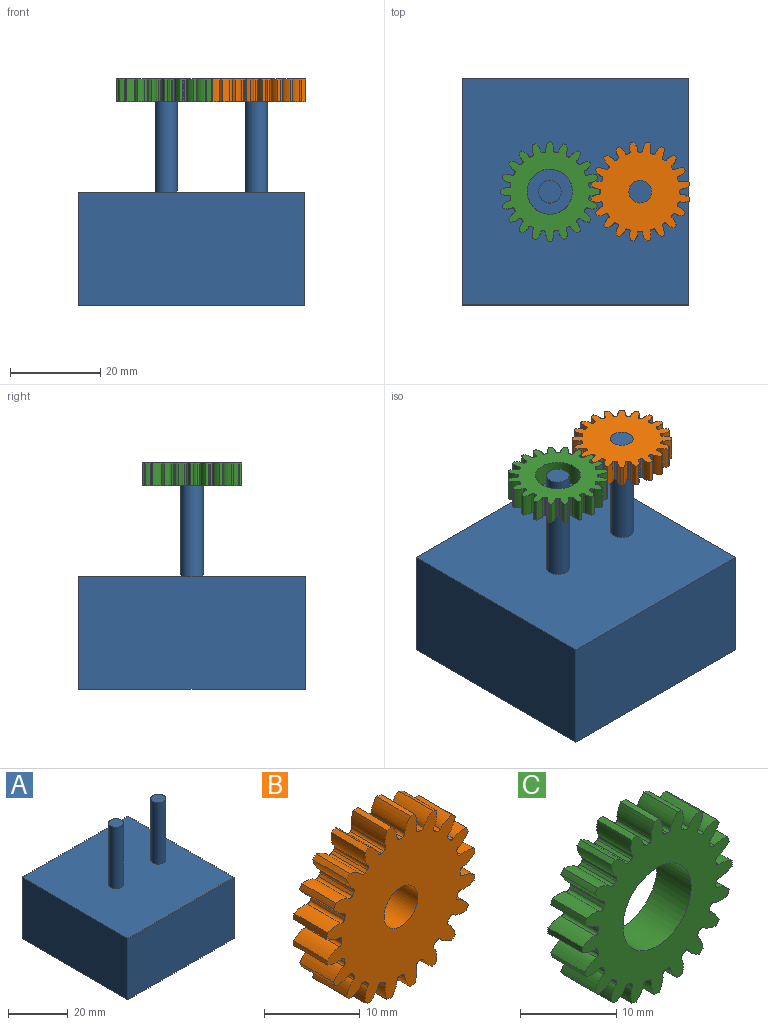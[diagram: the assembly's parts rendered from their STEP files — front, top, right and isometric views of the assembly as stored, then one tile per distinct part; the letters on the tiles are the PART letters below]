
ASSEMBLY  parts=3 mates=2
PART A: 10 faces, bbox 50x50x50 mm
  f0: plane 50x25mm, normal (-1,0,0), area 1250mm2, adj f1,f3,f4,f5
  f1: plane 50x25mm, normal (0,-1,0), area 1250mm2, adj f0,f2,f4,f5
  f2: plane 50x25mm, normal (1,0,0), area 1250mm2, adj f1,f3,f4,f5
  f3: plane 50x25mm, normal (0,1,0), area 1250mm2, adj f0,f2,f4,f5
  f4: plane 50x50mm, normal (0,0,1), area 2460.7mm2, adj f0,f1,f2,f3,f6,f8
  f5: plane 50x50mm, normal (0,0,-1), area 2500mm2, adj f0,f1,f2,f3
  f6: cylinder r=2.5mm len=25mm, axis (0,0,-1), area 392.7mm2, adj f4,f7
  f7: plane 5x5mm, normal (0,0,1), area 19.6mm2, adj f6
  f8: cylinder r=2.5mm len=25mm, axis (0,0,-1), area 392.7mm2, adj f4,f9
  f9: plane 5x5mm, normal (0,0,1), area 19.6mm2, adj f8
PART B: 123 faces, bbox 21.8x5x21.8 mm
  f0: extruded ~5x1.82mm, area 10.1mm2, adj f80,f81,f82,f83
  f1: cylinder r=8.75mm len=5mm, axis (0,1,0), area 2mm2, adj f81,f82,f83,f84
  f2: extruded ~5x1.82mm, area 10.1mm2, adj f3,f81,f82,f84
  f3: cylinder r=11mm len=5mm, axis (0,1,0), area 3.5mm2, adj f2,f4,f81,f82
  f4: extruded ~5x1.98mm, area 10.1mm2, adj f3,f81,f82,f85
  f5: cylinder r=8.75mm len=5mm, axis (0,1,0), area 2mm2, adj f81,f82,f85,f86
  f6: extruded ~5x1.48mm, area 10.1mm2, adj f7,f81,f82,f86
  f7: cylinder r=11mm len=5mm, axis (0,1,0), area 3.5mm2, adj f6,f8,f81,f82
  f8: extruded ~5x1.94mm, area 10.1mm2, adj f7,f81,f82,f87
  f9: cylinder r=8.75mm len=5mm, axis (0,1,0), area 2mm2, adj f81,f82,f87,f88
  f10: extruded ~5x1.71mm, area 10.1mm2, adj f11,f81,f82,f88
  f11: cylinder r=11mm len=5mm, axis (0,1,0), area 3.5mm2, adj f10,f12,f81,f82
  f12: extruded ~5x1.71mm, area 10.1mm2, adj f11,f81,f82,f89
  f13: cylinder r=8.75mm len=5mm, axis (0,1,0), area 2mm2, adj f81,f82,f89,f90
  f14: extruded ~5x1.94mm, area 10.1mm2, adj f15,f81,f82,f90
  f15: cylinder r=11mm len=5mm, axis (0,1,0), area 3.5mm2, adj f14,f16,f81,f82
  f16: extruded ~5x1.48mm, area 10.1mm2, adj f15,f81,f82,f91
  f17: cylinder r=8.75mm len=5mm, axis (0,1,0), area 2mm2, adj f81,f82,f91,f92
  f18: extruded ~5x1.98mm, area 10.1mm2, adj f19,f81,f82,f92
  f19: cylinder r=11mm len=5mm, axis (0,1,0), area 3.5mm2, adj f18,f20,f81,f82
  f20: extruded ~5x1.82mm, area 10.1mm2, adj f19,f81,f82,f93
  f21: cylinder r=8.75mm len=5mm, axis (0,1,0), area 2mm2, adj f81,f82,f93,f94
  f22: extruded ~5x1.82mm, area 10.1mm2, adj f23,f81,f82,f94
  f23: cylinder r=11mm len=5mm, axis (0,1,0), area 3.5mm2, adj f22,f24,f81,f82
  f24: extruded ~5x1.98mm, area 10.1mm2, adj f23,f81,f82,f95
  f25: cylinder r=8.75mm len=5mm, axis (0,1,0), area 2mm2, adj f81,f82,f95,f96
  f26: extruded ~5x1.48mm, area 10.1mm2, adj f27,f81,f82,f96
  f27: cylinder r=11mm len=5mm, axis (0,1,0), area 3.5mm2, adj f26,f28,f81,f82
  f28: extruded ~5x1.94mm, area 10.1mm2, adj f27,f81,f82,f97
  f29: cylinder r=8.75mm len=5mm, axis (0,1,0), area 2mm2, adj f81,f82,f97,f98
  f30: extruded ~5x1.71mm, area 10.1mm2, adj f31,f81,f82,f98
  f31: cylinder r=11mm len=5mm, axis (0,1,0), area 3.5mm2, adj f30,f32,f81,f82
  f32: extruded ~5x1.71mm, area 10.1mm2, adj f31,f81,f82,f99
  f33: cylinder r=8.75mm len=5mm, axis (0,1,0), area 2mm2, adj f81,f82,f99,f100
  f34: extruded ~5x1.94mm, area 10.1mm2, adj f35,f81,f82,f100
  f35: cylinder r=11mm len=5mm, axis (0,1,0), area 3.5mm2, adj f34,f36,f81,f82
  f36: extruded ~5x1.48mm, area 10.1mm2, adj f35,f81,f82,f101
  f37: cylinder r=8.75mm len=5mm, axis (0,1,0), area 2mm2, adj f81,f82,f101,f102
  f38: extruded ~5x1.98mm, area 10.1mm2, adj f39,f81,f82,f102
  f39: cylinder r=11mm len=5mm, axis (0,1,0), area 3.5mm2, adj f38,f40,f81,f82
  f40: extruded ~5x1.82mm, area 10.1mm2, adj f39,f81,f82,f103
  f41: cylinder r=8.75mm len=5mm, axis (0,1,0), area 2mm2, adj f81,f82,f103,f104
  f42: extruded ~5x1.82mm, area 10.1mm2, adj f43,f81,f82,f104
  f43: cylinder r=11mm len=5mm, axis (0,1,0), area 3.5mm2, adj f42,f44,f81,f82
  f44: extruded ~5x1.98mm, area 10.1mm2, adj f43,f81,f82,f105
  f45: cylinder r=8.75mm len=5mm, axis (0,1,0), area 2mm2, adj f81,f82,f105,f106
  f46: extruded ~5x1.48mm, area 10.1mm2, adj f47,f81,f82,f106
  f47: cylinder r=11mm len=5mm, axis (0,1,0), area 3.5mm2, adj f46,f48,f81,f82
  f48: extruded ~5x1.94mm, area 10.1mm2, adj f47,f81,f82,f107
  f49: cylinder r=8.75mm len=5mm, axis (0,1,0), area 2mm2, adj f81,f82,f107,f108
  f50: extruded ~5x1.71mm, area 10.1mm2, adj f51,f81,f82,f108
  f51: cylinder r=11mm len=5mm, axis (0,1,0), area 3.5mm2, adj f50,f52,f81,f82
  f52: extruded ~5x1.71mm, area 10.1mm2, adj f51,f81,f82,f109
  f53: cylinder r=8.75mm len=5mm, axis (0,1,0), area 2mm2, adj f81,f82,f109,f110
  f54: extruded ~5x1.94mm, area 10.1mm2, adj f55,f81,f82,f110
  f55: cylinder r=11mm len=5mm, axis (0,1,0), area 3.5mm2, adj f54,f56,f81,f82
  f56: extruded ~5x1.48mm, area 10.1mm2, adj f55,f81,f82,f111
  f57: cylinder r=8.75mm len=5mm, axis (0,1,0), area 2mm2, adj f81,f82,f111,f112
  f58: extruded ~5x1.98mm, area 10.1mm2, adj f59,f81,f82,f112
  f59: cylinder r=11mm len=5mm, axis (0,1,0), area 3.5mm2, adj f58,f60,f81,f82
  f60: extruded ~5x1.82mm, area 10.1mm2, adj f59,f81,f82,f113
  f61: cylinder r=8.75mm len=5mm, axis (0,1,0), area 2mm2, adj f81,f82,f113,f114
  f62: extruded ~5x1.82mm, area 10.1mm2, adj f63,f81,f82,f114
  f63: cylinder r=11mm len=5mm, axis (0,1,0), area 3.5mm2, adj f62,f64,f81,f82
  f64: extruded ~5x1.98mm, area 10.1mm2, adj f63,f81,f82,f115
  f65: cylinder r=8.75mm len=5mm, axis (0,1,0), area 2mm2, adj f81,f82,f115,f116
  f66: extruded ~5x1.48mm, area 10.1mm2, adj f67,f81,f82,f116
  f67: cylinder r=11mm len=5mm, axis (0,1,0), area 3.5mm2, adj f66,f68,f81,f82
  f68: extruded ~5x1.94mm, area 10.1mm2, adj f67,f81,f82,f117
  f69: cylinder r=8.75mm len=5mm, axis (0,1,0), area 2mm2, adj f81,f82,f117,f118
  f70: extruded ~5x1.71mm, area 10.1mm2, adj f71,f81,f82,f118
  f71: cylinder r=11mm len=5mm, axis (0,1,0), area 3.5mm2, adj f70,f72,f81,f82
  f72: extruded ~5x1.71mm, area 10.1mm2, adj f71,f81,f82,f119
  f73: cylinder r=8.75mm len=5mm, axis (0,1,0), area 2mm2, adj f81,f82,f119,f120
  f74: extruded ~5x1.94mm, area 10.1mm2, adj f75,f81,f82,f120
  f75: cylinder r=11mm len=5mm, axis (0,1,0), area 3.5mm2, adj f74,f76,f81,f82
  f76: extruded ~5x1.48mm, area 10.1mm2, adj f75,f81,f82,f121
  f77: cylinder r=8.75mm len=5mm, axis (0,1,0), area 2mm2, adj f81,f82,f121,f122
  f78: extruded ~5x1.98mm, area 10.1mm2, adj f80,f81,f82,f122
  f79: cylinder r=2.5mm len=5mm, axis (0,1,0), area 78.5mm2, adj f81,f82
  f80: cylinder r=11mm len=5mm, axis (0,1,0), area 3.5mm2, adj f0,f78,f81,f82
  f81: plane 21.84x21.84mm, normal (0,-1,0), area 288mm2, adj f0,f1,f2,f3,f4,f5,f6,f7
  f82: plane 21.84x21.84mm, normal (0,1,0), area 288mm2, adj f0,f1,f2,f3,f4,f5,f6,f7
  f83: cylinder r=0.37mm len=5mm, axis (0,1,0), area 2.8mm2, adj f0,f1,f81,f82
  f84: cylinder r=0.37mm len=5mm, axis (0,1,0), area 2.8mm2, adj f1,f2,f81,f82
  f85: cylinder r=0.37mm len=5mm, axis (0,1,0), area 2.8mm2, adj f4,f5,f81,f82
  f86: cylinder r=0.37mm len=5mm, axis (0,1,0), area 2.8mm2, adj f5,f6,f81,f82
  f87: cylinder r=0.37mm len=5mm, axis (0,1,0), area 2.8mm2, adj f8,f9,f81,f82
  f88: cylinder r=0.37mm len=5mm, axis (0,1,0), area 2.8mm2, adj f9,f10,f81,f82
  f89: cylinder r=0.37mm len=5mm, axis (0,1,0), area 2.8mm2, adj f12,f13,f81,f82
  f90: cylinder r=0.37mm len=5mm, axis (0,1,0), area 2.8mm2, adj f13,f14,f81,f82
  f91: cylinder r=0.37mm len=5mm, axis (0,1,0), area 2.8mm2, adj f16,f17,f81,f82
  f92: cylinder r=0.37mm len=5mm, axis (0,1,0), area 2.8mm2, adj f17,f18,f81,f82
  f93: cylinder r=0.37mm len=5mm, axis (0,1,0), area 2.8mm2, adj f20,f21,f81,f82
  f94: cylinder r=0.37mm len=5mm, axis (0,1,0), area 2.8mm2, adj f21,f22,f81,f82
  f95: cylinder r=0.37mm len=5mm, axis (0,1,0), area 2.8mm2, adj f24,f25,f81,f82
  f96: cylinder r=0.37mm len=5mm, axis (0,1,0), area 2.8mm2, adj f25,f26,f81,f82
  f97: cylinder r=0.37mm len=5mm, axis (0,1,0), area 2.8mm2, adj f28,f29,f81,f82
  f98: cylinder r=0.37mm len=5mm, axis (0,1,0), area 2.8mm2, adj f29,f30,f81,f82
  f99: cylinder r=0.37mm len=5mm, axis (0,1,0), area 2.8mm2, adj f32,f33,f81,f82
  f100: cylinder r=0.37mm len=5mm, axis (0,1,0), area 2.8mm2, adj f33,f34,f81,f82
  f101: cylinder r=0.37mm len=5mm, axis (0,1,0), area 2.8mm2, adj f36,f37,f81,f82
  f102: cylinder r=0.37mm len=5mm, axis (0,1,0), area 2.8mm2, adj f37,f38,f81,f82
  f103: cylinder r=0.37mm len=5mm, axis (0,1,0), area 2.8mm2, adj f40,f41,f81,f82
  f104: cylinder r=0.37mm len=5mm, axis (0,1,0), area 2.8mm2, adj f41,f42,f81,f82
  f105: cylinder r=0.37mm len=5mm, axis (0,1,0), area 2.8mm2, adj f44,f45,f81,f82
  f106: cylinder r=0.37mm len=5mm, axis (0,1,0), area 2.8mm2, adj f45,f46,f81,f82
  f107: cylinder r=0.37mm len=5mm, axis (0,1,0), area 2.8mm2, adj f48,f49,f81,f82
  f108: cylinder r=0.37mm len=5mm, axis (0,1,0), area 2.8mm2, adj f49,f50,f81,f82
  f109: cylinder r=0.37mm len=5mm, axis (0,1,0), area 2.8mm2, adj f52,f53,f81,f82
  f110: cylinder r=0.37mm len=5mm, axis (0,1,0), area 2.8mm2, adj f53,f54,f81,f82
  f111: cylinder r=0.37mm len=5mm, axis (0,1,0), area 2.8mm2, adj f56,f57,f81,f82
  f112: cylinder r=0.37mm len=5mm, axis (0,1,0), area 2.8mm2, adj f57,f58,f81,f82
  f113: cylinder r=0.37mm len=5mm, axis (0,1,0), area 2.8mm2, adj f60,f61,f81,f82
  f114: cylinder r=0.37mm len=5mm, axis (0,1,0), area 2.8mm2, adj f61,f62,f81,f82
  f115: cylinder r=0.37mm len=5mm, axis (0,1,0), area 2.8mm2, adj f64,f65,f81,f82
  f116: cylinder r=0.37mm len=5mm, axis (0,1,0), area 2.8mm2, adj f65,f66,f81,f82
  f117: cylinder r=0.37mm len=5mm, axis (0,1,0), area 2.8mm2, adj f68,f69,f81,f82
  f118: cylinder r=0.37mm len=5mm, axis (0,1,0), area 2.8mm2, adj f69,f70,f81,f82
  f119: cylinder r=0.37mm len=5mm, axis (0,1,0), area 2.8mm2, adj f72,f73,f81,f82
  f120: cylinder r=0.37mm len=5mm, axis (0,1,0), area 2.8mm2, adj f73,f74,f81,f82
  f121: cylinder r=0.37mm len=5mm, axis (0,1,0), area 2.8mm2, adj f76,f77,f81,f82
  f122: cylinder r=0.37mm len=5mm, axis (0,1,0), area 2.8mm2, adj f77,f78,f81,f82
PART C: 123 faces, bbox 22x5x22 mm
  f0: extruded ~5x1.92mm, area 10.1mm2, adj f79,f80,f81,f82
  f1: cylinder r=8.75mm len=5mm, axis (0,1,0), area 2mm2, adj f80,f81,f82,f83
  f2: extruded ~5x1.67mm, area 10.1mm2, adj f3,f80,f81,f83
  f3: cylinder r=11mm len=5mm, axis (0,1,0), area 3.5mm2, adj f2,f4,f80,f81
  f4: extruded ~5x1.98mm, area 10.1mm2, adj f3,f80,f81,f84
  f5: cylinder r=8.75mm len=5mm, axis (0,1,0), area 2mm2, adj f80,f81,f84,f85
  f6: extruded ~5x1.54mm, area 10.1mm2, adj f7,f80,f81,f85
  f7: cylinder r=11mm len=5mm, axis (0,1,0), area 3.5mm2, adj f6,f8,f80,f81
  f8: extruded ~5x1.85mm, area 10.1mm2, adj f7,f80,f81,f86
  f9: cylinder r=8.75mm len=5mm, axis (0,1,0), area 2mm2, adj f80,f81,f86,f87
  f10: extruded ~5x1.85mm, area 10.1mm2, adj f11,f80,f81,f87
  f11: cylinder r=11mm len=5mm, axis (0,1,0), area 3.5mm2, adj f10,f12,f80,f81
  f12: extruded ~5x1.54mm, area 10.1mm2, adj f11,f80,f81,f88
  f13: cylinder r=8.75mm len=5mm, axis (0,1,0), area 2mm2, adj f80,f81,f88,f89
  f14: extruded ~5x1.98mm, area 10.1mm2, adj f15,f80,f81,f89
  f15: cylinder r=11mm len=5mm, axis (0,1,0), area 3.5mm2, adj f14,f16,f80,f81
  f16: extruded ~5x1.67mm, area 10.1mm2, adj f15,f80,f81,f90
  f17: cylinder r=8.75mm len=5mm, axis (0,1,0), area 2mm2, adj f80,f81,f90,f91
  f18: extruded ~5x1.92mm, area 10.1mm2, adj f19,f80,f81,f91
  f19: cylinder r=11mm len=5mm, axis (0,1,0), area 3.5mm2, adj f18,f20,f80,f81
  f20: extruded ~5x1.92mm, area 10.1mm2, adj f19,f80,f81,f92
  f21: cylinder r=8.75mm len=5mm, axis (0,1,0), area 2mm2, adj f80,f81,f92,f93
  f22: extruded ~5x1.67mm, area 10.1mm2, adj f23,f80,f81,f93
  f23: cylinder r=11mm len=5mm, axis (0,1,0), area 3.5mm2, adj f22,f24,f80,f81
  f24: extruded ~5x1.98mm, area 10.1mm2, adj f23,f80,f81,f94
  f25: cylinder r=8.75mm len=5mm, axis (0,1,0), area 2mm2, adj f80,f81,f94,f95
  f26: extruded ~5x1.54mm, area 10.1mm2, adj f27,f80,f81,f95
  f27: cylinder r=11mm len=5mm, axis (0,1,0), area 3.5mm2, adj f26,f28,f80,f81
  f28: extruded ~5x1.85mm, area 10.1mm2, adj f27,f80,f81,f96
  f29: cylinder r=8.75mm len=5mm, axis (0,1,0), area 2mm2, adj f80,f81,f96,f97
  f30: extruded ~5x1.85mm, area 10.1mm2, adj f31,f80,f81,f97
  f31: cylinder r=11mm len=5mm, axis (0,1,0), area 3.5mm2, adj f30,f32,f80,f81
  f32: extruded ~5x1.54mm, area 10.1mm2, adj f31,f80,f81,f98
  f33: cylinder r=8.75mm len=5mm, axis (0,1,0), area 2mm2, adj f80,f81,f98,f99
  f34: extruded ~5x1.98mm, area 10.1mm2, adj f35,f80,f81,f99
  f35: cylinder r=11mm len=5mm, axis (0,1,0), area 3.5mm2, adj f34,f36,f80,f81
  f36: extruded ~5x1.67mm, area 10.1mm2, adj f35,f80,f81,f100
  f37: cylinder r=8.75mm len=5mm, axis (0,1,0), area 2mm2, adj f80,f81,f100,f101
  f38: extruded ~5x1.92mm, area 10.1mm2, adj f39,f80,f81,f101
  f39: cylinder r=11mm len=5mm, axis (0,1,0), area 3.5mm2, adj f38,f40,f80,f81
  f40: extruded ~5x1.92mm, area 10.1mm2, adj f39,f80,f81,f102
  f41: cylinder r=8.75mm len=5mm, axis (0,1,0), area 2mm2, adj f80,f81,f102,f103
  f42: extruded ~5x1.67mm, area 10.1mm2, adj f43,f80,f81,f103
  f43: cylinder r=11mm len=5mm, axis (0,1,0), area 3.5mm2, adj f42,f44,f80,f81
  f44: extruded ~5x1.98mm, area 10.1mm2, adj f43,f80,f81,f104
  f45: cylinder r=8.75mm len=5mm, axis (0,1,0), area 2mm2, adj f80,f81,f104,f105
  f46: extruded ~5x1.54mm, area 10.1mm2, adj f47,f80,f81,f105
  f47: cylinder r=11mm len=5mm, axis (0,1,0), area 3.5mm2, adj f46,f48,f80,f81
  f48: extruded ~5x1.85mm, area 10.1mm2, adj f47,f80,f81,f106
  f49: cylinder r=8.75mm len=5mm, axis (0,1,0), area 2mm2, adj f80,f81,f106,f107
  f50: extruded ~5x1.85mm, area 10.1mm2, adj f51,f80,f81,f107
  f51: cylinder r=11mm len=5mm, axis (0,1,0), area 3.5mm2, adj f50,f52,f80,f81
  f52: extruded ~5x1.54mm, area 10.1mm2, adj f51,f80,f81,f108
  f53: cylinder r=8.75mm len=5mm, axis (0,1,0), area 2mm2, adj f80,f81,f108,f109
  f54: extruded ~5x1.98mm, area 10.1mm2, adj f55,f80,f81,f109
  f55: cylinder r=11mm len=5mm, axis (0,1,0), area 3.5mm2, adj f54,f56,f80,f81
  f56: extruded ~5x1.67mm, area 10.1mm2, adj f55,f80,f81,f110
  f57: cylinder r=8.75mm len=5mm, axis (0,1,0), area 2mm2, adj f80,f81,f110,f111
  f58: extruded ~5x1.92mm, area 10.1mm2, adj f59,f80,f81,f111
  f59: cylinder r=11mm len=5mm, axis (0,1,0), area 3.5mm2, adj f58,f60,f80,f81
  f60: extruded ~5x1.92mm, area 10.1mm2, adj f59,f80,f81,f112
  f61: cylinder r=8.75mm len=5mm, axis (0,1,0), area 2mm2, adj f80,f81,f112,f113
  f62: extruded ~5x1.67mm, area 10.1mm2, adj f63,f80,f81,f113
  f63: cylinder r=11mm len=5mm, axis (0,1,0), area 3.5mm2, adj f62,f64,f80,f81
  f64: extruded ~5x1.98mm, area 10.1mm2, adj f63,f80,f81,f114
  f65: cylinder r=8.75mm len=5mm, axis (0,1,0), area 2mm2, adj f80,f81,f114,f115
  f66: extruded ~5x1.54mm, area 10.1mm2, adj f67,f80,f81,f115
  f67: cylinder r=11mm len=5mm, axis (0,1,0), area 3.5mm2, adj f66,f68,f80,f81
  f68: extruded ~5x1.85mm, area 10.1mm2, adj f67,f80,f81,f116
  f69: cylinder r=8.75mm len=5mm, axis (0,1,0), area 2mm2, adj f80,f81,f116,f117
  f70: extruded ~5x1.85mm, area 10.1mm2, adj f71,f80,f81,f117
  f71: cylinder r=11mm len=5mm, axis (0,1,0), area 3.5mm2, adj f70,f72,f80,f81
  f72: extruded ~5x1.54mm, area 10.1mm2, adj f71,f80,f81,f118
  f73: cylinder r=8.75mm len=5mm, axis (0,1,0), area 2mm2, adj f80,f81,f118,f119
  f74: extruded ~5x1.98mm, area 10.1mm2, adj f75,f80,f81,f119
  f75: cylinder r=11mm len=5mm, axis (0,1,0), area 3.5mm2, adj f74,f76,f80,f81
  f76: extruded ~5x1.67mm, area 10.1mm2, adj f75,f80,f81,f120
  f77: cylinder r=8.75mm len=5mm, axis (0,1,0), area 2mm2, adj f80,f81,f120,f121
  f78: extruded ~5x1.92mm, area 10.1mm2, adj f79,f80,f81,f121
  f79: cylinder r=11mm len=5mm, axis (0,1,0), area 3.5mm2, adj f0,f78,f80,f81
  f80: plane 22x22mm, normal (0,-1,0), area 229.1mm2, adj f0,f1,f2,f3,f4,f5,f6,f7
  f81: plane 22x22mm, normal (0,1,0), area 229.1mm2, adj f0,f1,f2,f3,f4,f5,f6,f7
  f82: cylinder r=0.37mm len=5mm, axis (0,1,0), area 2.8mm2, adj f0,f1,f80,f81
  f83: cylinder r=0.37mm len=5mm, axis (0,1,0), area 2.8mm2, adj f1,f2,f80,f81
  f84: cylinder r=0.37mm len=5mm, axis (0,1,0), area 2.8mm2, adj f4,f5,f80,f81
  f85: cylinder r=0.37mm len=5mm, axis (0,1,0), area 2.8mm2, adj f5,f6,f80,f81
  f86: cylinder r=0.37mm len=5mm, axis (0,1,0), area 2.8mm2, adj f8,f9,f80,f81
  f87: cylinder r=0.37mm len=5mm, axis (0,1,0), area 2.8mm2, adj f9,f10,f80,f81
  f88: cylinder r=0.37mm len=5mm, axis (0,1,0), area 2.8mm2, adj f12,f13,f80,f81
  f89: cylinder r=0.37mm len=5mm, axis (0,1,0), area 2.8mm2, adj f13,f14,f80,f81
  f90: cylinder r=0.37mm len=5mm, axis (0,1,0), area 2.8mm2, adj f16,f17,f80,f81
  f91: cylinder r=0.37mm len=5mm, axis (0,1,0), area 2.8mm2, adj f17,f18,f80,f81
  f92: cylinder r=0.37mm len=5mm, axis (0,1,0), area 2.8mm2, adj f20,f21,f80,f81
  f93: cylinder r=0.37mm len=5mm, axis (0,1,0), area 2.8mm2, adj f21,f22,f80,f81
  f94: cylinder r=0.37mm len=5mm, axis (0,1,0), area 2.8mm2, adj f24,f25,f80,f81
  f95: cylinder r=0.37mm len=5mm, axis (0,1,0), area 2.8mm2, adj f25,f26,f80,f81
  f96: cylinder r=0.37mm len=5mm, axis (0,1,0), area 2.8mm2, adj f28,f29,f80,f81
  f97: cylinder r=0.37mm len=5mm, axis (0,1,0), area 2.8mm2, adj f29,f30,f80,f81
  f98: cylinder r=0.37mm len=5mm, axis (0,1,0), area 2.8mm2, adj f32,f33,f80,f81
  f99: cylinder r=0.37mm len=5mm, axis (0,1,0), area 2.8mm2, adj f33,f34,f80,f81
  f100: cylinder r=0.37mm len=5mm, axis (0,1,0), area 2.8mm2, adj f36,f37,f80,f81
  f101: cylinder r=0.37mm len=5mm, axis (0,1,0), area 2.8mm2, adj f37,f38,f80,f81
  f102: cylinder r=0.37mm len=5mm, axis (0,1,0), area 2.8mm2, adj f40,f41,f80,f81
  f103: cylinder r=0.37mm len=5mm, axis (0,1,0), area 2.8mm2, adj f41,f42,f80,f81
  f104: cylinder r=0.37mm len=5mm, axis (0,1,0), area 2.8mm2, adj f44,f45,f80,f81
  f105: cylinder r=0.37mm len=5mm, axis (0,1,0), area 2.8mm2, adj f45,f46,f80,f81
  f106: cylinder r=0.37mm len=5mm, axis (0,1,0), area 2.8mm2, adj f48,f49,f80,f81
  f107: cylinder r=0.37mm len=5mm, axis (0,1,0), area 2.8mm2, adj f49,f50,f80,f81
  f108: cylinder r=0.37mm len=5mm, axis (0,1,0), area 2.8mm2, adj f52,f53,f80,f81
  f109: cylinder r=0.37mm len=5mm, axis (0,1,0), area 2.8mm2, adj f53,f54,f80,f81
  f110: cylinder r=0.37mm len=5mm, axis (0,1,0), area 2.8mm2, adj f56,f57,f80,f81
  f111: cylinder r=0.37mm len=5mm, axis (0,1,0), area 2.8mm2, adj f57,f58,f80,f81
  f112: cylinder r=0.37mm len=5mm, axis (0,1,0), area 2.8mm2, adj f60,f61,f80,f81
  f113: cylinder r=0.37mm len=5mm, axis (0,1,0), area 2.8mm2, adj f61,f62,f80,f81
  f114: cylinder r=0.37mm len=5mm, axis (0,1,0), area 2.8mm2, adj f64,f65,f80,f81
  f115: cylinder r=0.37mm len=5mm, axis (0,1,0), area 2.8mm2, adj f65,f66,f80,f81
  f116: cylinder r=0.37mm len=5mm, axis (0,1,0), area 2.8mm2, adj f68,f69,f80,f81
  f117: cylinder r=0.37mm len=5mm, axis (0,1,0), area 2.8mm2, adj f69,f70,f80,f81
  f118: cylinder r=0.37mm len=5mm, axis (0,1,0), area 2.8mm2, adj f72,f73,f80,f81
  f119: cylinder r=0.37mm len=5mm, axis (0,1,0), area 2.8mm2, adj f73,f74,f80,f81
  f120: cylinder r=0.37mm len=5mm, axis (0,1,0), area 2.8mm2, adj f76,f77,f80,f81
  f121: cylinder r=0.37mm len=5mm, axis (0,1,0), area 2.8mm2, adj f77,f78,f80,f81
  f122: cylinder r=5mm len=10mm, axis (0,1,0), area 157.1mm2, adj f80,f81
PLACE A t=(-25.1,-4.03,11.95)mm fixed
PLACE B rot(axis=(-1,0,0),90deg) t=(-29.53,-10.12,56.95)mm
PLACE C rot(axis=(-1,0,0),90deg) t=(-49.53,-10.12,56.95)mm
MATE revolute C.f3 <-> A.f6  axis (0,0,1) through (-49.53,-10.12,61.95)mm
MATE revolute B.f3 <-> A.f8  axis (0,0,1) through (-29.53,-10.12,61.95)mm
